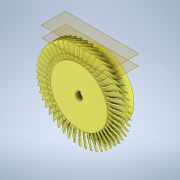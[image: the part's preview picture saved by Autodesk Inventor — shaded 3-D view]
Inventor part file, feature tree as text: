
AUTODESK INVENTOR PART (.ipt)
format: ipt  version: 2021.2 (Build 252289000, 289)  size: 2,797,568 bytes
history: native  units: in
note: dims shown in document units (in); Inventor stores cm internally (conversion verified against a paired STEP export)
features: sketch x5, extrude x4, plane x2, loft x1, pattern_circular x1, other x1
ambient origin geometry x8: Origin, YZ Plane, XZ Plane, XY Plane, X Axis, Y Axis, Z Axis, Center Point
bodies: Solid1 (feature_tree)
feature tree (14):
  extrude  "Extrusion1"  Depth=1.0in
  plane  "Work Plane1"
  extrude  "Extrusion2"  Depth=0.0312in
  plane  "Work Plane2"
  loft  "Loft3"
  pattern_circular  "Circular Pattern6"  Count=48 Angle=360.0deg
  extrude  "Extrusion3"  Depth=0.315in
  extrude  "Extrusion4"  Depth=0.125in
  sketch  "Sketch1"  dims[d0=2.6in d1=1.0in d2=0.0777in]
  sketch  "Sketch2"  dims[d3=1.5in d4=0.0312in]
  sketch  "Sketch4"  dims[d5=0.5in d6=0.0in d13=2.0in]
  other  "Edges3"
  sketch  "Sketch5"  dims[d28=0.0in d29=90.0deg]
  sketch  "Sketch6"  dims[d30=0.0in d31=90.0deg d35=18.8976in d36=360.0deg d38=0.315in d39=0.125in d40=0.125in d41=0.0in d42=0.0in d43=3.9375in d44=0.0in d45=0.0in]
